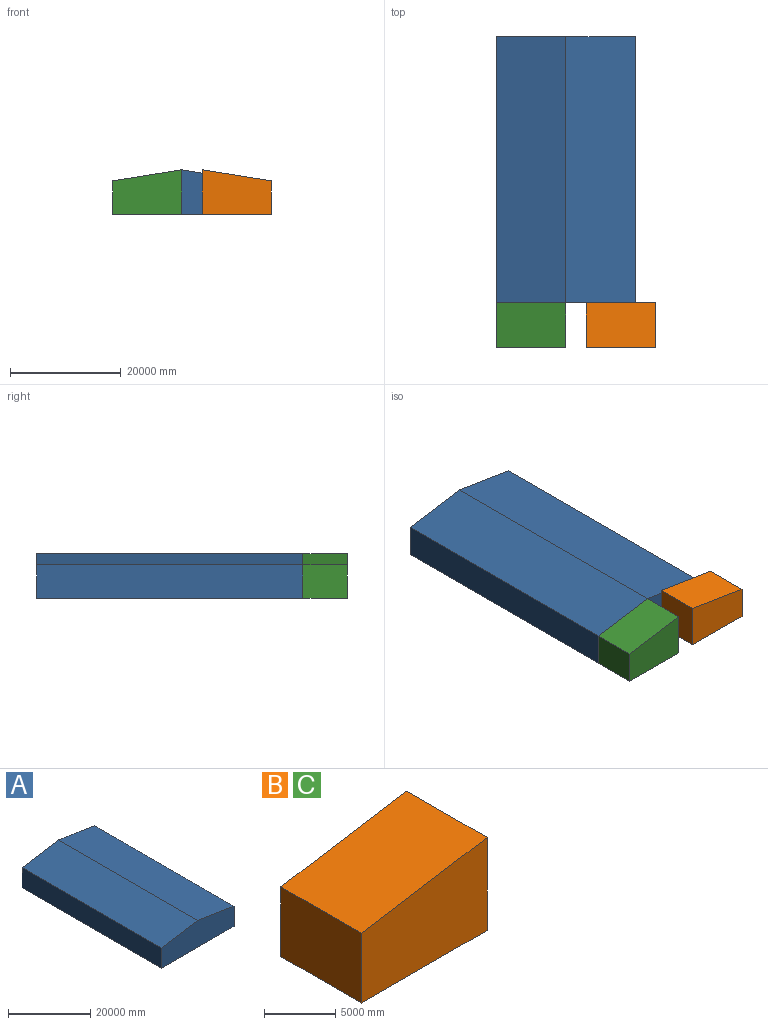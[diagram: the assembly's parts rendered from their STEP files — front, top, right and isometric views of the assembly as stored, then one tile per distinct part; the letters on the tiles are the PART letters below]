
ASSEMBLY  parts=3 mates=2
PART A: 7 faces, bbox 25000x48000x8000 mm
  f0: plane 48000x6000mm, normal (-1,0,0), area 288000000mm2, adj f1,f4,f5,f6
  f1: plane 48000x25000mm, normal (0,0,-1), area 1200000000mm2, adj f0,f2,f5,f6
  f2: plane 48000x6000mm, normal (1,0,0), area 288000000mm2, adj f1,f3,f5,f6
  f3: plane 48000x12500mm, normal (0.16,0,0.99), area 607631467.3mm2, adj f2,f4,f5,f6
  f4: plane 48000x12500mm, normal (-0.16,0,0.99), area 607631467.3mm2, adj f0,f3,f5,f6
  f5: plane 25000x8000mm, normal (0,1,0), area 175000000mm2, adj f0,f1,f2,f3,f4
  f6: plane 25000x8000mm, normal (0,-1,0), area 175000000mm2, adj f0,f1,f2,f3,f4
PART B: 6 faces, bbox 12500x8000x8000 mm
  f0: plane 8000x6000mm, normal (-1,0,0), area 48000000mm2, adj f1,f3,f4,f5
  f1: plane 12500x8000mm, normal (0,0,-1), area 100000000mm2, adj f0,f2,f4,f5
  f2: plane 8000x8000mm, normal (1,0,0), area 64000000mm2, adj f1,f3,f4,f5
  f3: plane 12500x8000mm, normal (-0.16,0,0.99), area 101271911.2mm2, adj f0,f2,f4,f5
  f4: plane 12500x8000mm, normal (0,1,0), area 87500000mm2, adj f0,f1,f2,f3
  f5: plane 12500x8000mm, normal (0,-1,0), area 87500000mm2, adj f0,f1,f2,f3
PART C: same geometry as B
PLACE A t=(-12445.74,-23861,-3838.49)mm fixed
PLACE B rot(axis=(0,0,1),180deg) t=(16198.66,-23861,-3838.49)mm
PLACE C t=(-12445.74,-31861,-3838.49)mm
MATE slider A.f2 <-> B.f0  axis (-1,0,0) through (12554.26,-23861,-3838.49)mm
MATE slider A.f0 <-> C.f0  axis (-1,0,0) through (-12445.74,-23861,-3838.49)mm
